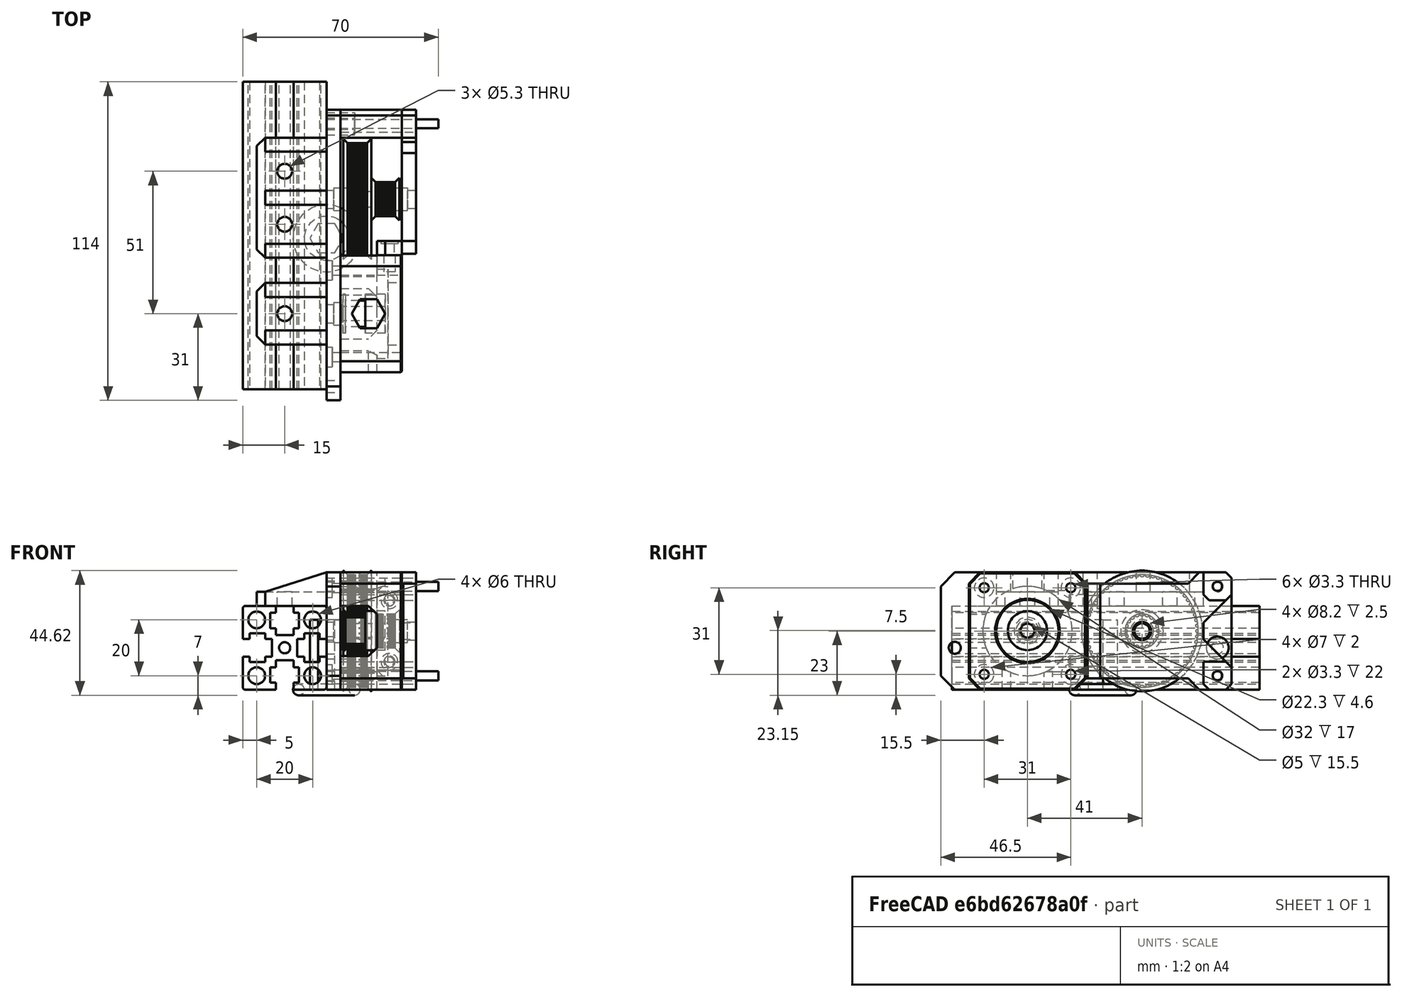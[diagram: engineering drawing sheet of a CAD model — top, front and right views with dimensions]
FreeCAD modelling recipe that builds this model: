
FCSTD DOCUMENT  (FreeCAD 0.18R16146 (Git))
Label: compact-z-belt
License: All rights reserved
LicenseURL: http://en.wikipedia.org/wiki/All_rights_reserved
objects: Part::Cylinder×37, Part::Cut×21, Part::Box×20, Part::Chamfer×20, Part::MultiFuse×17, Part::Feature×10, Mesh::Feature×1, Sketcher::SketchObject×1, PartDesign::Pad×1, PartDesign::Body×1, Part::Torus×1
note: 130 computed .brp shape members not serialized (recipe doc carries the construction recipe); baked Part::Feature solids carry a one-line shape summary decoded from their .brp

FEATURE [Part::Feature] Fusion041004010006  label="_3030-extrusion-003"
  shape: bbox 30 x 110 x 30 mm, 63 faces (baked)
FEATURE [Mesh::Feature] nema17_26mm  label="nema17-26mm"
  Placement = pos=(53.5,-16.25,78.8) rot=(0.707107,0,-0.707107;3.14159rad)
FEATURE [Part::Feature] Cut001002003001  label="64-20-bearing"
  Placement = pos=(6,14,21) rot=(0.707107,0,0.707107;3.14159rad)
  shape: bbox 20 x 43.24 x 43.24 mm, 2028 faces (baked)
FEATURE [Part::Feature] Cut002001  label="16-teeth-pulley"
  Placement = pos=(21,-27,21.15) rot=(0.707107,0,-0.707107;3.14159rad)
  shape: bbox 15.5 x 14 x 14 mm, 10 faces (baked)
FEATURE [Part::Box] Box  label="Cube"
  AttacherType = Attacher::AttachEngine3D
  Height = 42
  Length = 5
  Placement = pos=(0,-48,0) rot=(0,0,1;0rad)
  Width = 84
FEATURE [Part::Cylinder] Cylinder
  Angle = 360
  AttacherType = Attacher::AttachEngine3D
  Height = 10
  Placement = pos=(2.5,9,21) rot=(0,1,0;1.5708rad)
  Radius = 4.1
FEATURE [Part::Cylinder] Cylinder001
  Angle = 360
  AttacherType = Attacher::AttachEngine3D
  Height = 10
  Placement = pos=(2.5,-27,21) rot=(0,1,0;1.5708rad)
  Radius = 4.1
FEATURE [Part::Cylinder] Cylinder002
  Angle = 360
  AttacherType = Attacher::AttachEngine3D
  Height = 10
  Placement = pos=(-0.5,9,21) rot=(0,1,0;1.5708rad)
  Radius = 3.25
FEATURE [Part::Cylinder] Cylinder003
  Angle = 360
  AttacherType = Attacher::AttachEngine3D
  Height = 10
  Placement = pos=(-0.5,-27,21) rot=(0,1,0;1.5708rad)
  Radius = 3.25
FEATURE [Part::Box] Box001  label="Cube001"
  AttacherType = Attacher::AttachEngine3D
  Height = 42
  Length = 5
  Placement = pos=(22,-48,0) rot=(0,0,1;0rad)
  Width = 42
FEATURE [Part::MultiFuse] Fusion
  Placement = pos=(0,5,0) rot=(0,0,1;0rad)
  Shapes = -> [Cylinder002,Cylinder]
FEATURE [Part::MultiFuse] Fusion041004010007
  Shapes = -> [Cylinder001,Cylinder003]
FEATURE [Part::Cylinder] Cylinder004
  Angle = 360
  AttacherType = Attacher::AttachEngine3D
  Height = 25
  Placement = pos=(-3,-27,21) rot=(0,1,0;1.5708rad)
  Radius = 16
FEATURE [Part::Cylinder] Cylinder005
  Angle = 360
  AttacherType = Attacher::AttachEngine3D
  Height = 35
  Placement = pos=(-3,-11.5,36.5) rot=(0,1,0;1.5708rad)
  Radius = 1.65
FEATURE [Part::Cylinder] Cylinder006
  Angle = 360
  AttacherType = Attacher::AttachEngine3D
  Height = 35
  Placement = pos=(-3,-11.5,5.5) rot=(0,1,0;1.5708rad)
  Radius = 1.65
FEATURE [Part::Cylinder] Cylinder007
  Angle = 360
  AttacherType = Attacher::AttachEngine3D
  Height = 35
  Placement = pos=(-3,-42.5,36.5) rot=(0,1,0;1.5708rad)
  Radius = 1.65
FEATURE [Part::Cylinder] Cylinder008
  Angle = 360
  AttacherType = Attacher::AttachEngine3D
  Height = 35
  Placement = pos=(-3,-42.5,5.5) rot=(0,1,0;1.5708rad)
  Radius = 1.65
FEATURE [Part::Cylinder] Cylinder009
  Angle = 360
  AttacherType = Attacher::AttachEngine3D
  Height = 13
  Placement = pos=(5,14,21) rot=(0,1,0;1.5708rad)
  Radius = 23.5
FEATURE [Part::Box] Box002  label="Cube002"
  AttacherType = Attacher::AttachEngine3D
  Height = 42
  Length = 17
  Placement = pos=(5,-48,0) rot=(0,0,1;0rad)
  Width = 42
FEATURE [Part::Cylinder] Cylinder010
  Angle = 360
  AttacherType = Attacher::AttachEngine3D
  Height = 10
  Placement = pos=(22,-27,21) rot=(0,1,0;1.5708rad)
  Radius = 11.15
FEATURE [Part::Cut] Cut001002003003
  Base = -> Box001
  Tool = -> Cylinder010
FEATURE [Part::Cut] Cut001002003004
  Base = -> Box002
  Tool = -> Cylinder004
FEATURE [Part::Cut] Cut001002003006
  Base = -> Cut001002003004
  Tool = -> Cylinder009
FEATURE [Part::Box] Box003  label="Cube003"
  AttacherType = Attacher::AttachEngine3D
  Height = 34.3
  Length = 13
  Placement = pos=(5,-11.5,3.85) rot=(0,0,1;0rad)
  Width = 12
FEATURE [Part::Cylinder] Cylinder011
  Angle = 360
  AttacherType = Attacher::AttachEngine3D
  Height = 10
  Placement = pos=(22.5,2,10) rot=(1,0,0;1.5708rad)
  Radius = 1.65
FEATURE [Part::Cylinder] Cylinder012
  Angle = 360
  AttacherType = Attacher::AttachEngine3D
  Height = 10
  Placement = pos=(22.5,2,32) rot=(1,0,0;1.5708rad)
  Radius = 1.65
FEATURE [Part::Feature] Fusion041004010008001  label="Fusion041004010010"
  shape: bbox 4 x 10 x 26 mm, 6 faces, 2 solids (baked)
FEATURE [Part::Chamfer] Chamfer001
  Base = -> Cut001002003003
  Edges = 4 edges r=4: [Edge6,Edge8,Edge9,Edge11]
FEATURE [Part::Chamfer] Chamfer
  Base = -> Cut001002003006
  Edges = 4 edges r=4: [Edge8,Edge10,Edge15,Edge18]
FEATURE [Part::Box] Box004  label="Cube004"
  AttacherType = Attacher::AttachEngine3D
  Height = 31
  Length = 13
  Placement = pos=(5,-13.15,5.5) rot=(0,0,1;0rad)
  Width = 3.3
FEATURE [Part::Cylinder] Cylinder013
  Angle = 360
  AttacherType = Attacher::AttachEngine3D
  Height = 10
  Placement = pos=(-3,-11.5,36.5) rot=(0,1,0;1.5708rad)
  Radius = 1.65
FEATURE [Part::Cylinder] Cylinder014
  Angle = 360
  AttacherType = Attacher::AttachEngine3D
  Height = 10
  Placement = pos=(-3,-11.5,5.5) rot=(0,1,0;1.5708rad)
  Radius = 1.65
FEATURE [Part::Cylinder] Cylinder015
  Angle = 360
  AttacherType = Attacher::AttachEngine3D
  Height = 10
  Placement = pos=(-3,-42.5,5.5) rot=(0,1,0;1.5708rad)
  Radius = 1.65
FEATURE [Part::Cylinder] Cylinder016
  Angle = 360
  AttacherType = Attacher::AttachEngine3D
  Height = 10
  Placement = pos=(-3,-42.5,36.5) rot=(0,1,0;1.5708rad)
  Radius = 1.65
FEATURE [Part::Box] Box005  label="Cube005"
  AttacherType = Attacher::AttachEngine3D
  Height = 29
  Length = 13
  Placement = pos=(5,-26,6.5) rot=(0,0,1;0rad)
  Width = 24
FEATURE [Part::MultiFuse] Fusion041004010008004
  Shapes = -> [Chamfer001,Chamfer]
FEATURE [Part::Cut] Cut001002003007
  Base = -> Fusion041004010008004
  Tool = -> Fusion041004010008001
FEATURE [Sketcher::SketchObject] Sketch
  MapMode = 5
  Support = -> [XY_Plane]
  sketch-geometry (7):
    g0: LineSegment StartX=-6 StartY=0 StartZ=0 EndX=-3 EndY=-5.19615 EndZ=0
    g1: LineSegment StartX=-3 StartY=-5.19615 StartZ=0 EndX=3 EndY=-5.19615 EndZ=0
    g2: LineSegment StartX=3 StartY=-5.19615 StartZ=0 EndX=6 EndY=-9e-16 EndZ=0
    g3: LineSegment StartX=6 StartY=-9e-16 StartZ=0 EndX=3 EndY=5.19615 EndZ=0
    g4: LineSegment StartX=3 StartY=5.19615 StartZ=0 EndX=-3 EndY=5.19615 EndZ=0
    g5: LineSegment StartX=-3 StartY=5.19615 StartZ=0 EndX=-6 EndY=0 EndZ=0
    g6: Circle [constr] CenterX=0 CenterY=0 CenterZ=0 NormalX=0 NormalY=0 NormalZ=1 AngleXU=0 Radius=6
  constraints (13):
    c: Coincident(g0,g1)
    c: Coincident(g1,g2)
    c: Coincident(g2,g3)
    c: Coincident(g3,g4)
    c: Coincident(g4,g5)
    c: Coincident(g5,g0)
    c: Equal(g0, g1-g5) x5
    c: PointOnObject(g0,g6)
    c: PointOnObject(g1,g6)
    c: PointOnObject(g2,g6)
    c: PointOnObject(g3,g6)
    c: PointOnObject(g4,g6)
    c: PointOnObject(g5,g6)
FEATURE [PartDesign::Pad] Pad
  Length = 25
  Length2 = 100
  Profile = -> Sketch
  Type = 0
FEATURE [PartDesign::Body] Body
  Group = -> [Sketch,Pad]
  Origin = -> Origin
  Tip = -> Pad
FEATURE [Part::Feature] Pad001
  Placement = pos=(15,-27,19) rot=(0,0,1;0rad)
  shape: bbox 12 x 10.39 x 25 mm, 8 faces (baked)
FEATURE [Part::Cylinder] Cylinder024
  Angle = 360
  AttacherType = Attacher::AttachEngine3D
  Height = 2
  Placement = pos=(-3,-42.5,36.5) rot=(0,1,0;1.5708rad)
  Radius = 3.5
FEATURE [Part::Cylinder] Cylinder025
  Angle = 360
  AttacherType = Attacher::AttachEngine3D
  Height = 2
  Placement = pos=(-3,-42.5,5.5) rot=(0,1,0;1.5708rad)
  Radius = 3.5
FEATURE [Part::Cylinder] Cylinder026
  Angle = 360
  AttacherType = Attacher::AttachEngine3D
  Height = 2
  Placement = pos=(-3,-11.5,5.5) rot=(0,1,0;1.5708rad)
  Radius = 3.5
FEATURE [Part::Cylinder] Cylinder027
  Angle = 360
  AttacherType = Attacher::AttachEngine3D
  Height = 2
  Placement = pos=(-3,-11.5,36.5) rot=(0,1,0;1.5708rad)
  Radius = 3.5
FEATURE [Part::MultiFuse] Fusion041004010008009
  Shapes = -> [Fusion041004010007,Fusion]
FEATURE [Part::Cut] Cut
  Base = -> Box
  Tool = -> Fusion041004010008009
FEATURE [Part::MultiFuse] Fusion041004010008010
  Placement = pos=(3,0,0) rot=(0,0,1;0rad)
  Shapes = -> [Cylinder013,Cylinder014,Cylinder015,Cylinder016,Cylinder024,Cylinder027,Cylinder026,Cylinder025]
FEATURE [Part::Cut] Cut001002003012
  Base = -> Cut
  Tool = -> Fusion041004010008010
FEATURE [Part::MultiFuse] Fusion041004010008011
  Shapes = -> [Box004,Cylinder008,Cylinder005,Cylinder006,Cylinder007]
FEATURE [Part::Cut] Cut001002003013
  Base = -> Cut001002003007
  Tool = -> Fusion041004010008011
FEATURE [Part::Cut] Cut001002003014
  Base = -> Cut001002003013
  Tool = -> Box005
FEATURE [Part::Cut] Cut001002003015
  Base = -> Cut001002003014
  Tool = -> Box003
FEATURE [Part::Chamfer] Chamfer002
  Base = -> Cut001002003015
  Edges = 2 edges r=0.5: [Edge16,Edge33]
FEATURE [Part::Cut] Cut001002003016
  Base = -> Chamfer002
  Tool = -> Pad001
FEATURE [Part::Chamfer] Chamfer003
  Base = -> Cut001002003016
  Edges = 9 edges r=0.4: [Edge117,Edge118,Edge119,Edge120,Edge121,Edge122,Edge123,Edge124,Edge125]
FEATURE [Part::Box] Box006  label="Cube006"
  AttacherType = Attacher::AttachEngine3D
  Height = 34
  Length = 14
  Placement = pos=(18,-6,4) rot=(0,0,1;0rad)
  Width = 5
FEATURE [Part::Cylinder] Cylinder028
  Angle = 360
  AttacherType = Attacher::AttachEngine3D
  Height = 10
  Placement = pos=(22.5,2,10) rot=(1,0,0;1.5708rad)
  Radius = 3
FEATURE [Part::Cylinder] Cylinder029
  Angle = 360
  AttacherType = Attacher::AttachEngine3D
  Height = 10
  Placement = pos=(22.5,2,32) rot=(1,0,0;1.5708rad)
  Radius = 3
FEATURE [Part::MultiFuse] Fusion041004010008013
  Placement = pos=(0,6,0) rot=(0,0,1;0rad)
  Shapes = -> [Cylinder029,Cylinder028]
FEATURE [Part::Box] Box007  label="Cube007"
  AttacherType = Attacher::AttachEngine3D
  Height = 34
  Length = 14
  Placement = pos=(27,-10.5,4) rot=(0,0,1;0rad)
  Width = 5
FEATURE [Part::Chamfer] Chamfer004
  Base = -> Box007
  Edges = 1 edges r=0.5: [Edge3]
FEATURE [Part::MultiFuse] Fusion041004010008014
  Shapes = -> [Cylinder012,Cylinder011]
FEATURE [Part::MultiFuse] Fusion041004010008015
  Shapes = -> [Fusion041004010008014,Fusion041004010008013]
FEATURE [Part::Cut] Cut001002003017
  Base = -> Box006
  Tool = -> Chamfer004
FEATURE [Part::Cut] Cut001002003018
  Base = -> Cut001002003017
  Tool = -> Fusion041004010008015
FEATURE [Part::Chamfer] Chamfer005
  Base = -> Cut001002003018
  Edges = 2 edges r=3: [Edge2,Edge4]
FEATURE [Part::Box] Box008  label="Cube008"
  AttacherType = Attacher::AttachEngine3D
  Height = 42
  Length = 5
  Placement = pos=(27,-5.5,0) rot=(0,0,1;0rad)
  Width = 51.5
FEATURE [Part::Cylinder] Cylinder030
  Angle = 360
  AttacherType = Attacher::AttachEngine3D
  Height = 10
  Placement = pos=(-1.1e-15,41,5) rot=(0,1,0;1.5708rad)
  Radius = 2
FEATURE [Part::Cylinder] Cylinder031
  Angle = 360
  AttacherType = Attacher::AttachEngine3D
  Height = 10
  Placement = pos=(-8.2e-15,41,37) rot=(0,1,0;1.5708rad)
  Radius = 2
FEATURE [Part::Cylinder] Cylinder032
  Angle = 360
  AttacherType = Attacher::AttachEngine3D
  Height = 10
  Placement = pos=(-3.3e-15,41,15) rot=(0,1,0;1.5708rad)
  Radius = 4
FEATURE [Part::Cylinder] Cylinder033
  Angle = 360
  AttacherType = Attacher::AttachEngine3D
  Height = 10
  Placement = pos=(-3e-15,-53,15) rot=(0,1,0;1.5708rad)
  Radius = 2.15
FEATURE [Part::Box] Box009  label="Cube009"
  AttacherType = Attacher::AttachEngine3D
  Height = 42
  Length = 5
  Placement = pos=(0,36,0) rot=(0,0,1;0rad)
  Width = 10
FEATURE [Part::Box] Box010  label="Cube010"
  AttacherType = Attacher::AttachEngine3D
  Height = 42
  Length = 5
  Placement = pos=(0,-58,0) rot=(0,0,1;0rad)
  Width = 10
FEATURE [Part::Cut] Cut001002003019
  Base = -> Box010
  Tool = -> Cylinder033
FEATURE [Part::Cylinder] Cylinder034
  Angle = 360
  AttacherType = Attacher::AttachEngine3D
  Height = 10
  Placement = pos=(-3e-15,41,15) rot=(0,1,0;1.5708rad)
  Radius = 2.15
FEATURE [Part::Cylinder] Cylinder035
  Angle = 360
  AttacherType = Attacher::AttachEngine3D
  Height = 10
  Placement = pos=(-8.2e-15,41,37) rot=(0,1,0;1.5708rad)
  Radius = 2
FEATURE [Part::Cylinder] Cylinder036
  Angle = 360
  AttacherType = Attacher::AttachEngine3D
  Height = 10
  Placement = pos=(-1.1e-15,41,5) rot=(0,1,0;1.5708rad)
  Radius = 2
FEATURE [Part::MultiFuse] Fusion041004010008016
  Shapes = -> [Cylinder036,Cylinder035,Cylinder034]
FEATURE [Part::Cut] Cut001002003020
  Base = -> Box009
  Tool = -> Fusion041004010008016
FEATURE [Part::Chamfer] Chamfer006
  Base = -> Cut001002003019
  Edges = 1 edges r=5: [Edge6]
FEATURE [Part::Box] Box011  label="Cube011"
  AttacherType = Attacher::AttachEngine3D
  Height = 26
  Length = 5
  Placement = pos=(27,51,8) rot=(0,0,1;0rad)
  Width = 51.5
FEATURE [Part::Box] Box012  label="Cube012"
  AttacherType = Attacher::AttachEngine3D
  Height = 5
  Length = 5
  Placement = pos=(27,-5.5,-1) rot=(0,0,1;0rad)
  Width = 40
FEATURE [Part::Box] Box013  label="Cube013"
  AttacherType = Attacher::AttachEngine3D
  Height = 5
  Length = 5
  Placement = pos=(27,-5.5,38) rot=(0,0,1;0rad)
  Width = 40
FEATURE [Part::Chamfer] Chamfer008
  Base = -> Box013
  Edges = 1 edges r=4: [Edge11]
FEATURE [Part::Chamfer] Chamfer009
  Base = -> Box012
  Edges = 1 edges r=4: [Edge12]
FEATURE [Part::Box] Box014  label="Cube014"
  AttacherType = Attacher::AttachEngine3D
  Height = 10
  Length = 27
  Placement = pos=(5,36,0) rot=(0,0,1;0rad)
  Width = 10
FEATURE [Part::Box] Box015  label="Cube015"
  AttacherType = Attacher::AttachEngine3D
  Height = 10
  Length = 27
  Placement = pos=(5,36,32) rot=(0,0,1;0rad)
  Width = 10
FEATURE [Part::Cylinder] Cylinder039
  Angle = 360
  AttacherType = Attacher::AttachEngine3D
  Height = 40
  Placement = pos=(-8.2e-15,41,37) rot=(0,1,0;1.5708rad)
  Radius = 1.65
FEATURE [Part::Cylinder] Cylinder040
  Angle = 360
  AttacherType = Attacher::AttachEngine3D
  Height = 40
  Placement = pos=(-1.1e-15,41,5) rot=(0,1,0;1.5708rad)
  Radius = 1.65
FEATURE [Part::Chamfer] Chamfer017
  Base = -> Cut001002003020
  Edges = 1 edges r=2: [Edge13]
FEATURE [Part::Chamfer] Chamfer018
  Base = -> Box011
  Edges = 2 edges r=10: [Edge9,Edge10]
  Placement = pos=(0,-15,0) rot=(0,0,1;0rad)
FEATURE [Part::Cut] Cut001002003026
  Base = -> Box008
  Tool = -> Chamfer018
FEATURE [Part::Cut] Cut001002003027
  Base = -> Cut001002003026
  Tool = -> Chamfer008
FEATURE [Part::Cut] Cut001002003028
  Base = -> Cut001002003027
  Tool = -> Chamfer009
FEATURE [Part::Chamfer] Chamfer019
  Base = -> Box015
  Edges = 3 edges r=2: [Edge9,Edge11,Edge12]
FEATURE [Part::Chamfer] Chamfer020
  Base = -> Box014
  Edges = 3 edges r=2: [Edge9,Edge11,Edge12]
FEATURE [Part::Chamfer] Chamfer021
  Base = -> Cut001002003028
  Edges = 2 edges r=2: [Edge13,Edge25]
FEATURE [Part::Cylinder] Cylinder041
  Angle = 360
  AttacherType = Attacher::AttachEngine3D
  Height = 8
  Placement = pos=(26,14,21) rot=(0,1,0;1.5708rad)
  Radius = 3.25
FEATURE [Part::Cylinder] Cylinder042
  Angle = 360
  AttacherType = Attacher::AttachEngine3D
  Height = 3
  Placement = pos=(26,14,21) rot=(0,1,0;1.5708rad)
  Radius = 4.1
FEATURE [Part::MultiFuse] Fusion041004010008017
  Shapes = -> [Cylinder041,Cylinder042]
FEATURE [Part::Cut] Cut001002003031
  Base = -> Chamfer021
  Tool = -> Fusion041004010008017
FEATURE [Part::Chamfer] Chamfer022
  Base = -> Chamfer017
  Edges = 1 edges r=2: [Edge17]
FEATURE [Part::Chamfer] Chamfer023
  Base = -> Chamfer006
  Edges = 1 edges r=5: [Edge9]
FEATURE [Part::MultiFuse] Fusion041004010008018
  Shapes = -> [Chamfer023,Cut001002003012,Chamfer022]
FEATURE [Part::Box] Box016  label="Cube016"
  AttacherType = Attacher::AttachEngine3D
  Height = 5
  Length = 25
  Placement = pos=(-25,-38,30) rot=(0,0,1;0rad)
  Width = 22
FEATURE [Part::Box] Box017  label="Cube017"
  AttacherType = Attacher::AttachEngine3D
  Height = 5
  Length = 25
  Placement = pos=(-25,-7,30) rot=(0,0,1;0rad)
  Width = 43
FEATURE [Part::Cylinder] Cylinder044
  Angle = 360
  AttacherType = Attacher::AttachEngine3D
  Height = 10
  Placement = pos=(-15,-27,30) rot=(0,0,1;0rad)
  Radius = 2.65
FEATURE [Part::Box] Box018  label="Cube018"
  AttacherType = Attacher::AttachEngine3D
  Height = 8
  Length = 23
  Placement = pos=(-22,-38,34) rot=(0,0,1;0rad)
  Width = 5
FEATURE [Part::Cylinder] Cylinder045
  Angle = 360
  AttacherType = Attacher::AttachEngine3D
  Height = 10
  Placement = pos=(-15,5,30) rot=(0,0,1;0rad)
  Radius = 2.65
FEATURE [Part::Cylinder] Cylinder046
  Angle = 360
  AttacherType = Attacher::AttachEngine3D
  Height = 10
  Placement = pos=(-15,24,30) rot=(0,0,1;0rad)
  Radius = 2.65
FEATURE [Part::Chamfer] Chamfer024
  Base = -> Box018
  Edges = 1 edges: [Edge2 r1=7 r2=22]
FEATURE [Part::Chamfer] Chamfer025
  Base = -> Box017
  Edges = 2 edges r=3: [Edge1,Edge3]
FEATURE [Part::Chamfer] Chamfer026
  Base = -> Box016
  Edges = 2 edges r=3: [Edge1,Edge3]
FEATURE [Part::Feature] Chamfer024001  label="Chamfer027"
  Placement = pos=(0,17,0) rot=(0,0,1;0rad)
  shape: bbox 23 x 5 x 8 mm, 7 faces (baked)
FEATURE [Part::Feature] Chamfer024002  label="Chamfer028"
  Placement = pos=(0,31,0) rot=(0,0,1;0rad)
  shape: bbox 23 x 5 x 8 mm, 7 faces (baked)
FEATURE [Part::Feature] Chamfer024003  label="Chamfer029"
  Placement = pos=(0,69,0) rot=(0,0,1;0rad)
  shape: bbox 23 x 5 x 8 mm, 7 faces (baked)
FEATURE [Part::Feature] Chamfer024004  label="Chamfer030"
  Placement = pos=(0,50,0) rot=(0,0,1;0rad)
  shape: bbox 23 x 5 x 8 mm, 7 faces (baked)
FEATURE [Part::MultiFuse] Fusion041004010008019
  Shapes = -> [Chamfer024001,Chamfer026,Chamfer024]
FEATURE [Part::MultiFuse] Fusion041004010008020
  Shapes = -> [Chamfer024002,Chamfer025,Chamfer024004,Chamfer024003]
FEATURE [Part::MultiFuse] Fusion041004010008021
  Shapes = -> [Fusion041004010008020,Fusion041004010008019]
FEATURE [Part::MultiFuse] Fusion041004010008022
  Shapes = -> [Fusion041004010008018,Fusion041004010008021]
FEATURE [Part::Torus] Torus  label="83-teerh-3gt-belt"
  Angle1 = -180
  Angle2 = 180
  Angle3 = 360
  AttacherType = Attacher::AttachEngine3D
  Radius1 = 10
  Radius2 = 2
FEATURE [Part::Box] Box019  label="Cube019"
  AttacherType = Attacher::AttachEngine3D
  Height = 10
  Length = 13
  Placement = pos=(5,-36,0) rot=(0,0,1;0rad)
  Width = 18
FEATURE [Part::Chamfer] Chamfer024005
  Base = -> Box019
  Edges = 2 edges r=3: [Edge5,Edge7]
FEATURE [Part::Cut] Cut001002003032
  Base = -> Chamfer003
  Tool = -> Chamfer024005
FEATURE [Part::Feature] Chamfer024005001  label="Chamfer024006"
  Placement = pos=(0,-49,-6) rot=(1,0,0;4.71239rad)
  shape: bbox 13 x 10 x 18 mm, 8 faces (baked)
FEATURE [Part::Cut] Cut001002003033
  Base = -> Cut001002003032
  Tool = -> Chamfer024005001
FEATURE [Part::MultiFuse] Fusion041004010008023
  Shapes = -> [Cylinder044,Cylinder045,Cylinder046]
FEATURE [Part::Cut] Cut001002003034
  Base = -> Fusion041004010008022
  Tool = -> Fusion041004010008023
